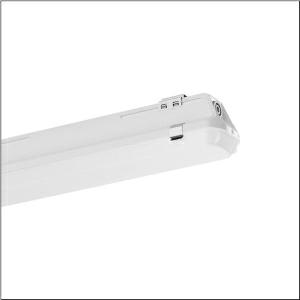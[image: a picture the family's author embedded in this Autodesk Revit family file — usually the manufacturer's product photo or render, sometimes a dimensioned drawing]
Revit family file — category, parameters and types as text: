
# Revit family: monsun_r__21_emergency_51fb10dp487b3h_7346
name_source: partatom
category: Lighting Fixtures
units: mm (PartAtom-declared; Revit-internal decimal feet)

## family parameters
Cut with Voids When Loaded = No
Host = Face
Light Source = No
Part Type = Normal
Room Calculation Point = No
Round Connector Dimension = Use Diameter
Shared = No

## types (1)
- --- (1 x LED, 8090 lm, 57.2 W, 4000K)
    Apparent Load = 57 VA
    CIE Flux Codes = 47 77 93 94 100
    Color Rendering = 80
    Color Temperature = 4000K
    Default Elevation = 1800 mm
    Description = Monsun® 21 emergency, damp-proof luminaire, chain hanger, primary optical cover: enclosure, of PMMA, light emission: direct distribution, primary light characteristic: symmetric, installation type: vertical mounting, horizontal mounting, surface-mounted, suspended mounting, LED, rated luminous flux: 8.090lm, luminous efficacy: 141lm/W, light colour: 840, colour temperature: 4000K, control gear: ECG DALI, with terminal, 5+3-pole, max. 2.5mm², mains connection: 220..240V, AC, 50/60Hz, rated input power: 57W, control gear: single battery element, battery: NiCd, 4,5Ah, mains connection: 230V, housing, of glass-fibre reinforced polyester, uncoated, bright grey, incl. chain hanger, length: 1.590mm, width: 90mm, height: 88mm, clip for enclosure, of stainless steel (V2A), ceiling mounting element, of stainless steel (V2A), chain hanger, of stainless steel (V2A), protection rating (complete): IP66, insulation class (complete): insulation class I (protective earthing), certification: CE, UKCA, protection symbol: D, impact resistance: IK04, permissible operating ambient temperature: +5..+25°C, standard: EN 60598-2-1, EN 50419, EN 60598-2-22, corresponds to IFS (International Featured Standards) requirements for safety and quality in the food industry, for indoor or canopied outdoor use, no direct snow, no direct sun, no direct rain, contact your sales advisor before using the luminaires in applications with unclear chemical exposure, large temperature fluctuations or condensation-forming humidity, LABS conformity tested according to VDMA 24364:2018-05, packaging unit: 1 piece
    Height = 89 mm
    Lamp = 1 x LED
    Lamp Light Flux = 8090 lm
    Lamp Power = 57.2 W
    Lamp count = 1
    Length = 1590 mm
    Luminous efficacy = 141 lm/W
    Manufacturer = Siteco
    ModVariant = No
    Model = 51FB10DP487B3H
    Mounting Place = Ceiling
    Mounting Type = Surface mounted
    Number of Poles = 1
    OnlyDefault = Yes
    Power Factor = 1
    Product Name = Monsun® 21 emergency
    Product group = damp-proof luminaire
    ProductGroupID = 301
    Protection Class = Protection class I
    Protection Degree = IP 66
    RLX_Detail_Level = 1
    RLX_Emergency_Light_Flux = 0 lm
    RLX_Emergency_Type = 0
    RLX_Emergency_Type_DB = No
    RlxData = <blob elided: 92397 chars, md5=ba86e8f4>
    Socket = socket
    Standby Power = 0 W
    System Light Flux = 8090 lm
    System Power = 57 W
    Type Comments = factory setting: luminous flux: 100 % | dim-lin: 254 | 358 mA
    Type Image = l_1006717.jpg
    URL = http://relux.com
    VarID = @adj_151955
    Voltage = 0 V
    Weight = 0.00 kg
    Width = 90 mm

## geometry (parser evidence)
native form markers: Blend x4, Sweep x14
no freeform markers — native parametric forms only
